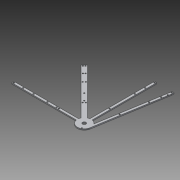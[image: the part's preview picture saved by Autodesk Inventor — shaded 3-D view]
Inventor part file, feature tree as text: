
AUTODESK INVENTOR PART (.ipt)
format: ipt  version: 2014 SP1 (Build 180222100, 222)  size: 239,616 bytes
history: native  units: in
note: dims shown in document units (in); Inventor stores cm internally (conversion verified against a paired STEP export)
features: extrude x4, sketch x4, reference x2
ambient origin geometry x8: Origin, YZ Plane, XZ Plane, XY Plane, X Axis, Y Axis, Z Axis, Center Point
bodies: Body1 (feature_tree)
feature tree (10):
  extrude  "Extrusion2"  Depth=1.5in
  extrude  "Extrusion8"  Depth=0.25in
  extrude  "Extrusion9"  Depth=5.5in
  extrude  "Extrusion10"  Depth=0.25in
  sketch  "Sketch1"  dims[d0=0.5in d1=4.0in d2=0.5in d3=0.5in d4=1.5in d5=1.5in d6=1.5in d7=0.25in d8=0.25in d9=0.25in d10=0.5in d11=0.5in d12=3.75in d14=0.266in d15=0.266in d16=0.266in d17=0.25in d18=0.266in d19=0.25in d20=0.25in d21=0.266in d22=0.266in d23=0.266in d24=0.25in d25=0.25in d26=0.266in d28=1.125in d30=0.266in d32=0.266in d33=0.25in d36=1.5in]
  sketch  "Sketch6"  dims[d37=1.0in d38=0.25in]
  sketch  "Sketch8"  dims[d39=5.5in d40=2.1762in]
  sketch  "Sketch9"  dims[d41=5.5in d42=0.25in d43=0.25in d44=0.2874in d45=10.926in d46=10.6389in d47=0.2871in d48=0.2871in d49=15.5in d50=15.5in d51=0.25in d52=0.5in d53=0.266in d54=0.25in d55=0.266in d56=0.266in d57=15.5in d58=0.25in d60=0.266in d61=0.25in d62=0.266in d63=0.266in d64=0.266in d65=0.266in d66=2.0in d67=2.0in d68=2.0in d71=0.297in d72=0.297in d73=0.297in d74=0.297in d75=2.0in d77=0.0in d78=0.25in d79=0.25in d80=0.0in d115=0.266in d117=0.266in d118=9.75in d122=6.0in d123=8.0in d124=0.266in d126=6.0in d127=8.0in d129=0.25in d130=0.25in d131=0.25in d132=0.25in d133=1.0in d134=0.0in d135=0.748in d136=0.25in d137=0.0in d138=1.0in d139=0.0in]
  reference  "Reference1"
  reference  "Reference3"
